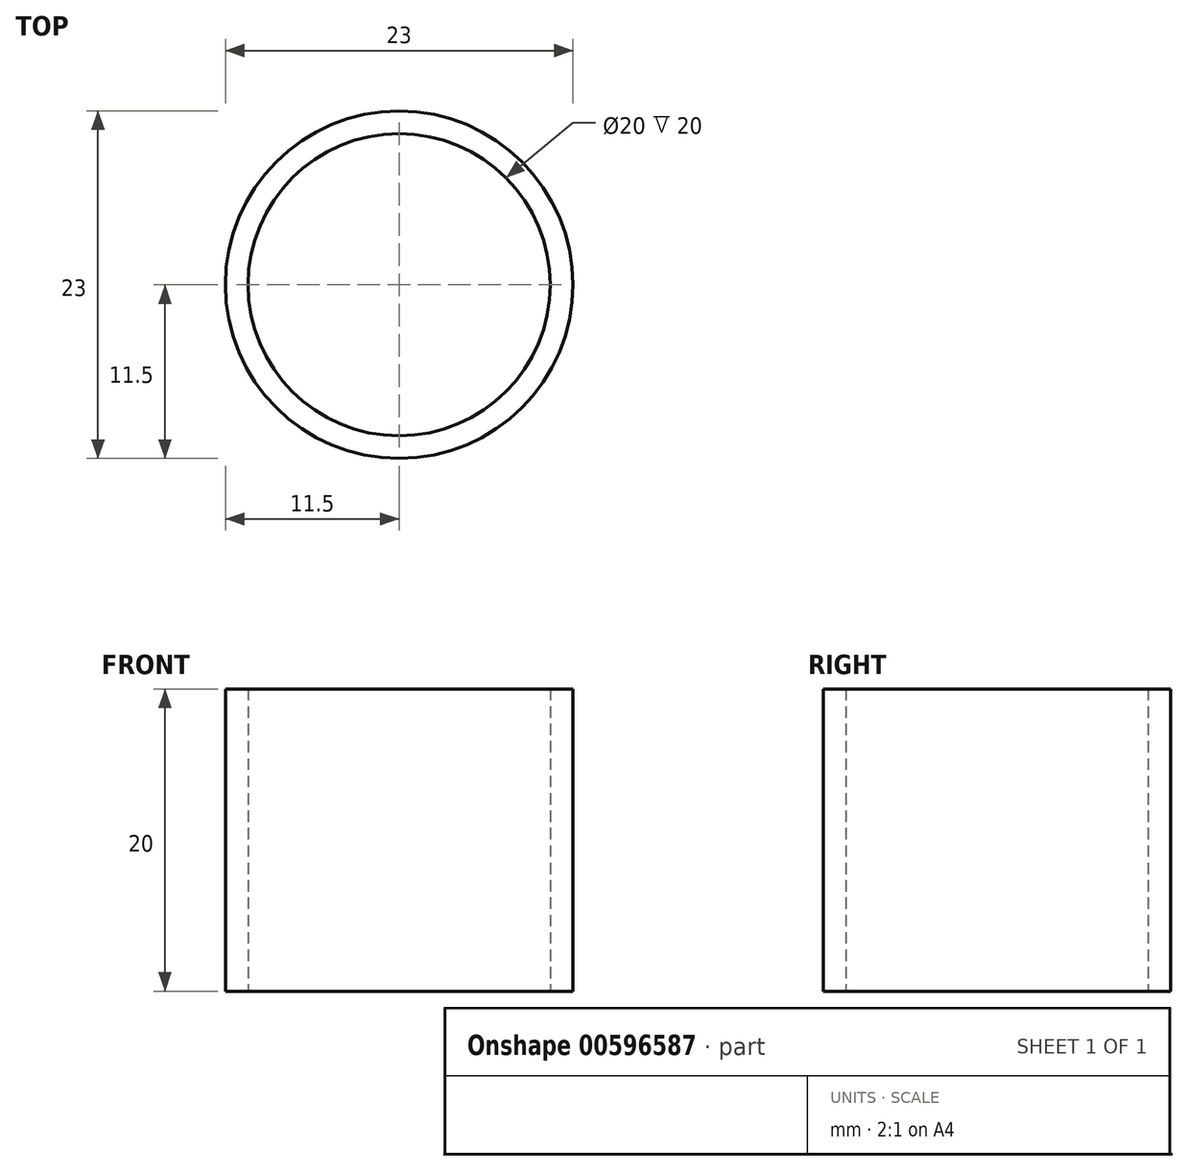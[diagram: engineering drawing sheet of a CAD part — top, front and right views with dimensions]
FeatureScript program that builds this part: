
annotation { "Feature Type Name" : "Feature", "Feature Type Description" : "" }
export const myFeature = defineFeature(function(context is Context, id is Id, definition is map)
    precondition{}
    {
        {
            var Q0;
            Q0=qCreatedBy(makeId("Top.planeOp"),FACE);
            var sketch = newSketch(context, id + "F0", { "sketchPlane" : qUnion([Q0])});
            skCircle(sketch, "E0", {"center": v(0, 0) * mm, "radius": 11.5 * mm});
            skCircle(sketch, "E1", {"center": v(0, 0) * mm, "radius": 10 * mm});
            skSolve(sketch);
        }
        {
            var Q0;
            Q0=makeQuery(id+"F0.imprint","IMPRINT",FACE,{"disambiguationData":[TD([[makeQuery(id+"F0.imprint","IMPRINT",EDGE,{"derivedFrom":sQuery(id+"F0.wireOp",EDGE,"E0")}),1.0]])]});
            extrude(context, id + "F1", {"entities" : qUnion([Q0]), "depth" : 20 * mm, "offsetDistance" : 25 * mm});
        }
    });
